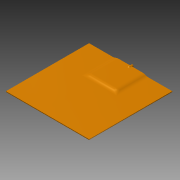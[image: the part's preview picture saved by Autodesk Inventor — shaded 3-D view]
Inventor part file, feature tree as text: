
AUTODESK INVENTOR PART (.ipt)
format: ipt  version: 2013 (Build 170138000, 138)  size: 172,032 bytes
history: native  units: mm
features: fillet x5, extrude x4, sketch x4
ambient origin geometry x8: Origin, YZ Plane, XZ Plane, XY Plane, X Axis, Y Axis, Z Axis, Center Point
bodies: Solid1 (feature_tree)
feature tree (13):
  extrude  "Extrusion1"  Depth=2.0mm TaperAngle=0.0deg
  extrude  "Extrusion2"  Depth=3.5mm TaperAngle=0.0deg
  extrude  "Extrusion3"  Depth=5.0mm TaperAngle=0.0deg
  extrude  "Extrusion4"  Depth=7.5mm TaperAngle=0.0deg
  fillet  "Fillet1"  Radius=2.0mm
  fillet  "Fillet2"  Radius=3.8mm
  fillet  "Fillet3"  Radius=1.0mm
  fillet  "Fillet4"  Radius=20.0mm
  fillet  "Fillet5"  Radius=20.0mm
  sketch  "Sketch1"  dims[d0=225.0mm d1=2.0mm d2=0.0mm]
  sketch  "Sketch2"  dims[d3=75.0mm d5=3.5mm d6=0.0mm]
  sketch  "Sketch3"  dims[d7=6.0mm d9=5.0mm d10=0.0mm]
  sketch  "Sketch4"  dims[d11=1.0mm d12=7.5mm d13=0.0mm d14=2.0mm d15=3.8mm d16=1.0mm d17=20.0mm d18=20.0mm]
